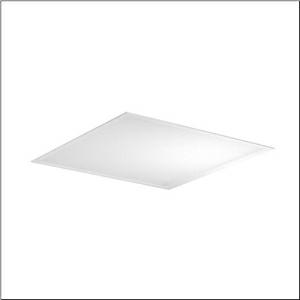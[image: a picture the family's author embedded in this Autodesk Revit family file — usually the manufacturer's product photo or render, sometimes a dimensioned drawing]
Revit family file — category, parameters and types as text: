
# Revit family: apollon_21_square_51mq12wd2454
name_source: partatom
category: Lighting Fixtures
units: mm (PartAtom-declared; Revit-internal decimal feet)

## family parameters
Cut with Voids When Loaded = No
Host = Face
Light Source = No
Part Type = Normal
Room Calculation Point = No
Round Connector Dimension = Use Diameter
Shared = No

## types (1)
- Apollon 21 square (1 x LED, 4200 lm, 24.7 W, 4000K)
    Apparent Load = 25 VA
    CIE Flux Codes = 60 87 97 100 100
    Color Rendering = 80
    Color Temperature = 4000K
    Default Elevation = 1800 mm
    Description = Apollon 21 square, office luminaire, primary optical cover: micro prismatic cover, of PMMA, CAT 2 (L<= 3000cd/m²), light emission: direct distribution, primary light characteristic: symmetric, installation type: lay-in mounting, recessed, LED, rated luminous flux: 4.200lm, luminous efficacy: 170lm/W, light colour: 840, colour temperature: 4000K, control gear: DALI 2, Multilumen, with terminal, 5-pole, mains connection: 220..240V, AC/DC, 0/50..60Hz, rated input power: 24.7W, suitable for self-contained emergency lighting element 59MQE002602A with integrated self-test function according to EN 60598-2-22, housing, of aluminium, coated, traffic white (RAL 9016), module: M600, length: 595mm, width: 595mm, height: 55mm, housing upper side, of sheet steel, galvanised, protection rating (complete): IP20, protection rating (lamp compartment, on room side): IP54, insulation class (complete): insulation class II (safety insulation), certification: CE, ENEC, UKCA, impact resistance: IK03, permissible operating ambient temperature: -20..+45°C, standard: EN 60598-2-22, corresponds to IFS (International Featured Standards) requirements for safety and quality in the food industry, packaging unit: 1 piece
    Height = 0 mm  [stored 0 ft]
    Lamp = 1 x LED
    Lamp Light Flux = 4200 lm
    Lamp Power = 24.7 W
    Lamp count = 1
    Length = 595 mm
    Luminous efficacy = 170 lm/W
    Manufacturer = Siteco
    ModVariant = No
    Model = 51MQ12WD2454
    Mounting Place = Ceiling
    Mounting Type = Recessed
    Number of Poles = 1
    OnlyDefault = Yes
    Power Factor = 1
    Product Name = Apollon 21 square
    Product group = office luminaire | ceiling recessed
    ProductGroupID = 400
    Protection Class = Protection class II
    Protection Degree = IP 20
    RLX_Detail_Level = 1
    RLX_Emergency_Light_Flux = 0 lm
    RLX_Emergency_Type = 0
    RLX_Emergency_Type_DB = No
    RlxData = <blob elided: 97109 chars, md5=1ffdee87>
    Socket = socket
    Standby Power = 0 W
    System Light Flux = 4200 lm
    System Power = 25 W
    Type Comments = Product without accessories
    Type Image = l_1291049.jpg
    URL = http://relux.com
    VarID = ---
    Voltage = 0 V
    Weight = 0.00 kg
    Width = 595 mm

note: [stored X ft] marks values corroborated as IEEE doubles in the binary element streams (Revit-internal decimal feet)

## geometry (parser evidence)
native form markers: Blend x4, Sweep x9
no freeform markers — native parametric forms only
